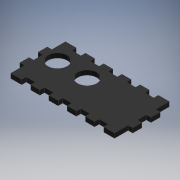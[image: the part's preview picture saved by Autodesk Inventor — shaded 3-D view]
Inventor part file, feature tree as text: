
AUTODESK INVENTOR PART (.ipt)
format: ipt  version: 2019 (Build 230136000, 136)  size: 202,240 bytes
history: native  units: mm
features: extrude x2, sketch x2
ambient origin geometry x8: Origin, YZ Plane, XZ Plane, XY Plane, X Axis, Y Axis, Z Axis, Center Point
bodies: Solid1 (feature_tree)
feature tree (4):
  extrude  "Extrusion1"  Depth=48.0mm
  extrude  "Extrusion2"  Depth=4.0mm
  sketch  "Sketch1"  dims[d0=99.0mm d1=48.0mm]
  sketch  "Sketch2"  dims[d2=17.0mm d3=15.0mm d4=30.0mm d5=26.0mm d6=4.0mm d7=0.0mm d8=4.0mm d11=8.0mm d12=4.0mm d14=8.0mm d15=8.0mm d16=8.0mm d17=4.0mm d18=8.0mm d19=4.0mm d20=0.0mm]
